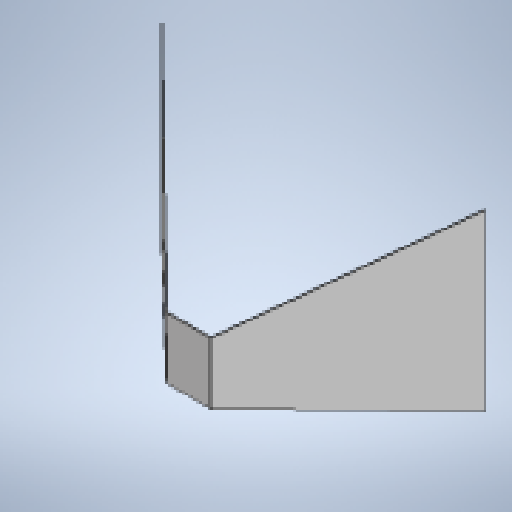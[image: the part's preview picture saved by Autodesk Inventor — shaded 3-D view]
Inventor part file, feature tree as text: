
AUTODESK INVENTOR PART (.ipt)
format: ipt  version: 2025 (Build 290162010, 162A)  size: 307,712 bytes
history: native  units: mm
features: other x4, sheet_metal_op x3, sketch x3, extrude x1, mirror x1, projected_geometry x1
ambient origin geometry x8: Origin, YZ Plane, XZ Plane, XY Plane, X Axis, Y Axis, Z Axis, Center Point
bodies: Solid1 (feature_tree)
feature tree (13):
  sheet_metal_op  "Contour Flange1"
  extrude  "Extrusion3"  Depth=3.0mm
  mirror  "Mirror3"
  other  "A-Side Definition"
  other  "Mark2"
  sketch  "Sketch1"  dims[d7=3.0mm d8=3.0mm]
  other  "Plate1"
  sheet_metal_op  "Bend1"
  sheet_metal_op  "Corner1"
  sketch  "Sketch7"  dims[d9=1.5mm]
  projected_geometry  "Projected Loop2"
  sketch  "Sketch8"  dims[d10=6.0mm d11=3.0mm d12=800.0mm d13=3.0mm d14=3.0mm d15=12.0mm d16=3.0mm d17=3.0mm d38=6.0mm d39=3.0mm d40=3.0mm d44=3.0mm d73=6.0mm d74=742.222353mm d75=23.736478mm d77=3.0mm d78=3.0mm d82=887.0mm d84=6.981317mm d85=0.0mm d86=0.0mm d88=100.0mm]
  other  "Definition1"
